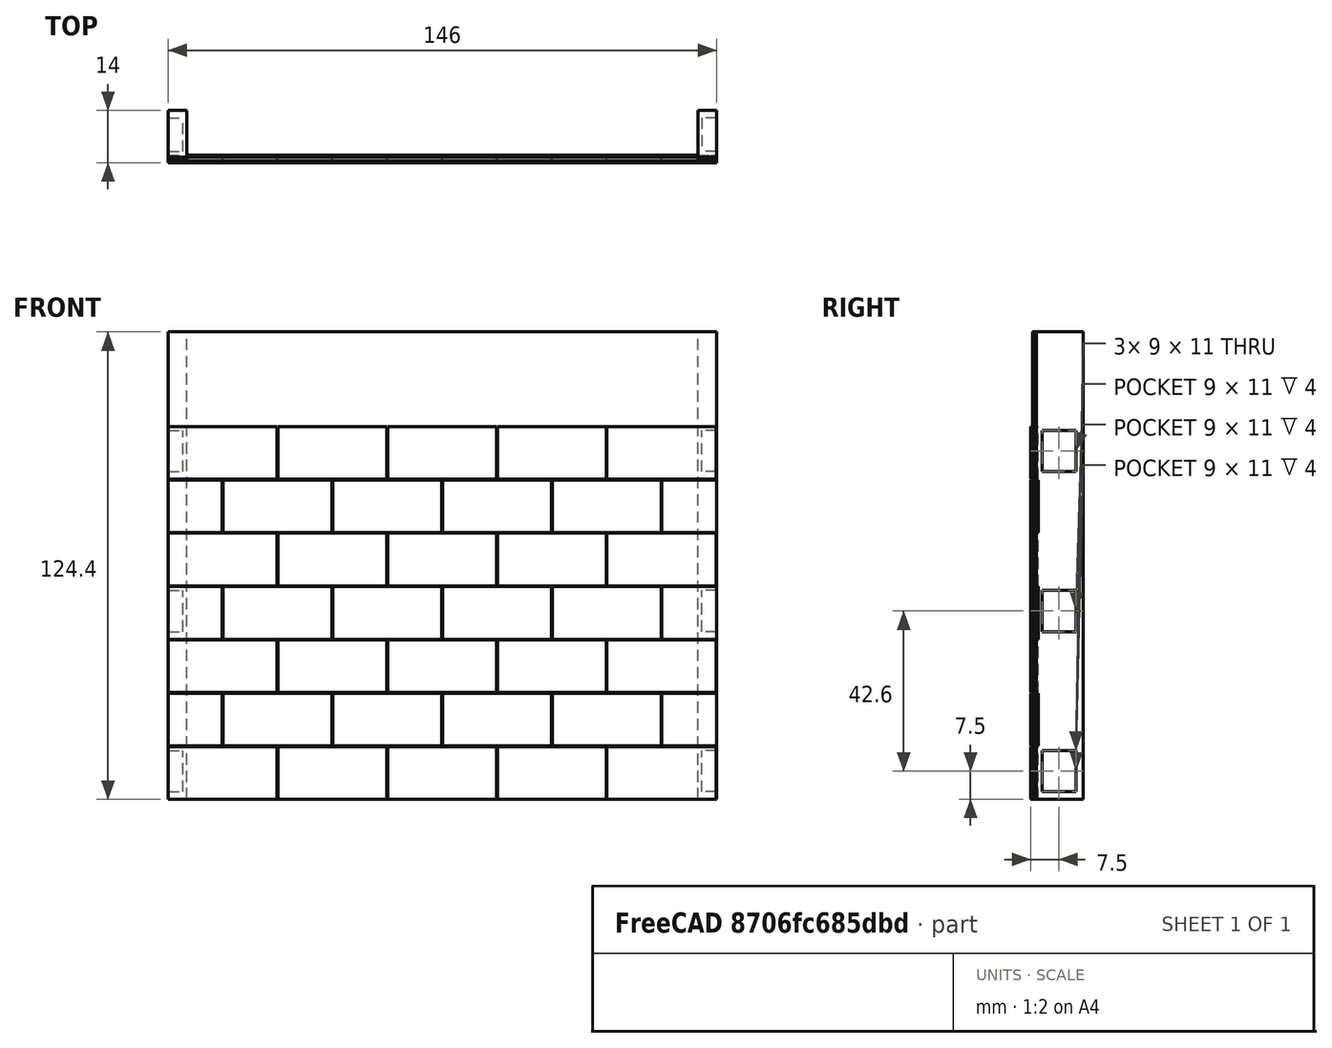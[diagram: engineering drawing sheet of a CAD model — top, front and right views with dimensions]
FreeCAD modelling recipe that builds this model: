
FCSTD DOCUMENT  (FreeCAD 0.16R6707 (Git))
Label: Muro_castillo_playmobil
License: CreativeCommons Attribution-ShareAlike
LicenseURL: http://creativecommons.org/licenses/by-sa/4.0/
objects: Part::Box×6, Part::FeaturePython×4, Part::MultiFuse×2, Part::Cut×2
note: 14 computed .brp shape members not serialized (recipe doc carries the construction recipe); baked Part::Feature solids carry a one-line shape summary decoded from their .brp

FEATURE [Part::Box] Box  label="Ladrillo_base"
  Height = 14
  Length = 29
  Width = 2
FEATURE [Part::FeaturePython] Array  label="Pared1"  # Draft array (typed FeaturePython)
  Angle = 360
  ArrayType = 0
  Axis = (0,0,1)
  Base = -> Box
  Center = (0,0,0)
  Fuse = false
  IntervalAxis = (0,0,0)
  IntervalX = (29.2,0,0)
  IntervalY = (0,1,0)
  IntervalZ = (14.6,0,14.2)
  NumberPolar = 1
  NumberX = 5
  NumberY = 1
  NumberZ = 7
FEATURE [Part::FeaturePython] Array001  label="Pared2"  # Draft array (typed FeaturePython)
  Angle = 360
  ArrayType = 0
  Axis = (0,0,1)
  Base = -> Box
  Center = (0,0,0)
  Fuse = false
  IntervalAxis = (0,0,0)
  IntervalX = (29.2,0,0)
  IntervalY = (0,1,0)
  IntervalZ = (-14.6,0,14.2)
  NumberPolar = 1
  NumberX = 6
  NumberY = 1
  NumberZ = 7
FEATURE [Part::MultiFuse] Fusion  label="Pared_ladrillos"
  Shapes = -> [Array,Array001]
FEATURE [Part::Box] Box001  label="Fondo_pared"
  Height = 124.4
  Length = 146
  Placement = pos=(0,0.5,0) rot=(0,0,1;0rad)
  Width = 1
  expr: Height = 14.2 * 7 + 25
  expr: Length = 29.2 * 5
FEATURE [Part::Box] Box002  label="Borrar_labrillos1"
  Height = 99.4
  Length = 87.6
  Placement = pos=(-87.6,0,0) rot=(0,0,1;0rad)
  Width = 2
  expr: Length = 29.2 * 3
FEATURE [Part::Box] Box003  label="Borrar_ladrillos2"
  Height = 99.4
  Length = 87.6
  Placement = pos=(146,0,0) rot=(0,0,1;0rad)
  Width = 2
  expr: Length = 29.2 * 3
FEATURE [Part::MultiFuse] Fusion001  label="Borrar_ladrillos"
  Shapes = -> [Box003,Box002]
FEATURE [Part::Cut] Cut  label="Pared_ladrillos_final"
  Base = -> Fusion
  Tool = -> Fusion001
FEATURE [Part::Box] Box004  label="Lateral"
  Height = 124.4
  Length = 5
  Width = 13
FEATURE [Part::Box] Box005  label="Ensamblaje"
  Height = 11
  Length = 4
  Placement = pos=(0,2,2) rot=(0,0,1;0rad)
  Width = 9
FEATURE [Part::FeaturePython] Array002  label="Emsamblajes3"  # Draft array (typed FeaturePython)
  Angle = 360
  ArrayType = 0
  Axis = (0,0,1)
  Base = -> Box005
  Center = (0,0,0)
  Fuse = false
  IntervalAxis = (0,0,0)
  IntervalX = (1,0,0)
  IntervalY = (0,1,0)
  IntervalZ = (0,0,42.6)
  NumberPolar = 1
  NumberX = 1
  NumberY = 1
  NumberZ = 3
  expr: IntervalZ.z = 14.2 * 3
FEATURE [Part::Cut] Cut001  label="Lateral_final"
  Base = -> Box004
  Placement = pos=(0,1,0) rot=(0,0,1;0rad)
  Tool = -> Array002
FEATURE [Part::FeaturePython] Array003  label="Las_dos_paredes_laterales"  # Draft array (typed FeaturePython)
  Angle = 360
  ArrayType = 1
  Axis = (0,0,1)
  Base = -> Cut001
  Center = (73,7.5,0)
  Fuse = false
  IntervalAxis = (0,0,0)
  IntervalX = (1,0,0)
  IntervalY = (0,1,0)
  IntervalZ = (0,0,0)
  NumberPolar = 2
  NumberX = 2
  NumberY = 2
  NumberZ = 1
